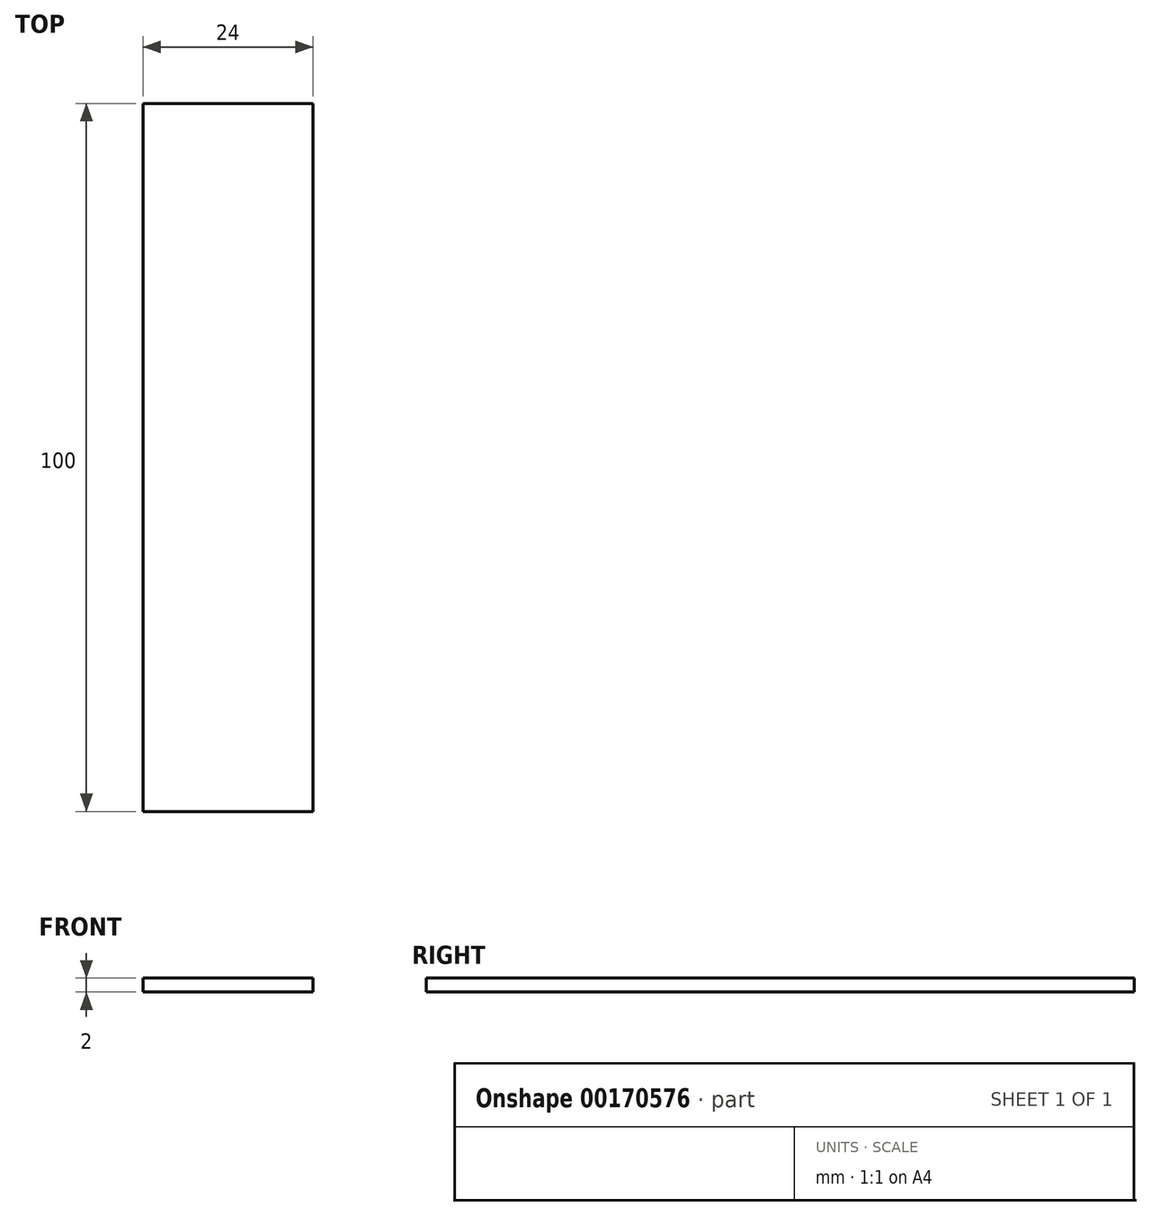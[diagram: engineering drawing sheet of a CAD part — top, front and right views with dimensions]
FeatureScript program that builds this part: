
annotation { "Feature Type Name" : "Feature", "Feature Type Description" : "" }
export const myFeature = defineFeature(function(context is Context, id is Id, definition is map)
    precondition{}
    {
        {
            var Q0;
            Q0=qCreatedBy(makeId("Top.planeOp"),FACE);
            var sketch = newSketch(context, id + "F0", { "sketchPlane" : qUnion([Q0])});
            skLineSegment(sketch, "E0.bottom", {"start": v(-12, 50) * mm, "end": v(12, 50) * mm});
            skLineSegment(sketch, "E0.top", {"start": v(-12, -50) * mm, "end": v(12, -50) * mm});
            skLineSegment(sketch, "E0.left", {"start": v(-12, 50) * mm, "end": v(-12, -50) * mm});
            skLineSegment(sketch, "E0.right", {"start": v(12, 50) * mm, "end": v(12, -50) * mm});
            skSolve(sketch);
        }
        {
            var Q0;
            Q0 = qSketchRegion(id + "F0", true);
            extrude(context, id + "F1", {"entities" : qUnion([Q0]), "depth" : 2 * mm});
        }
    });
